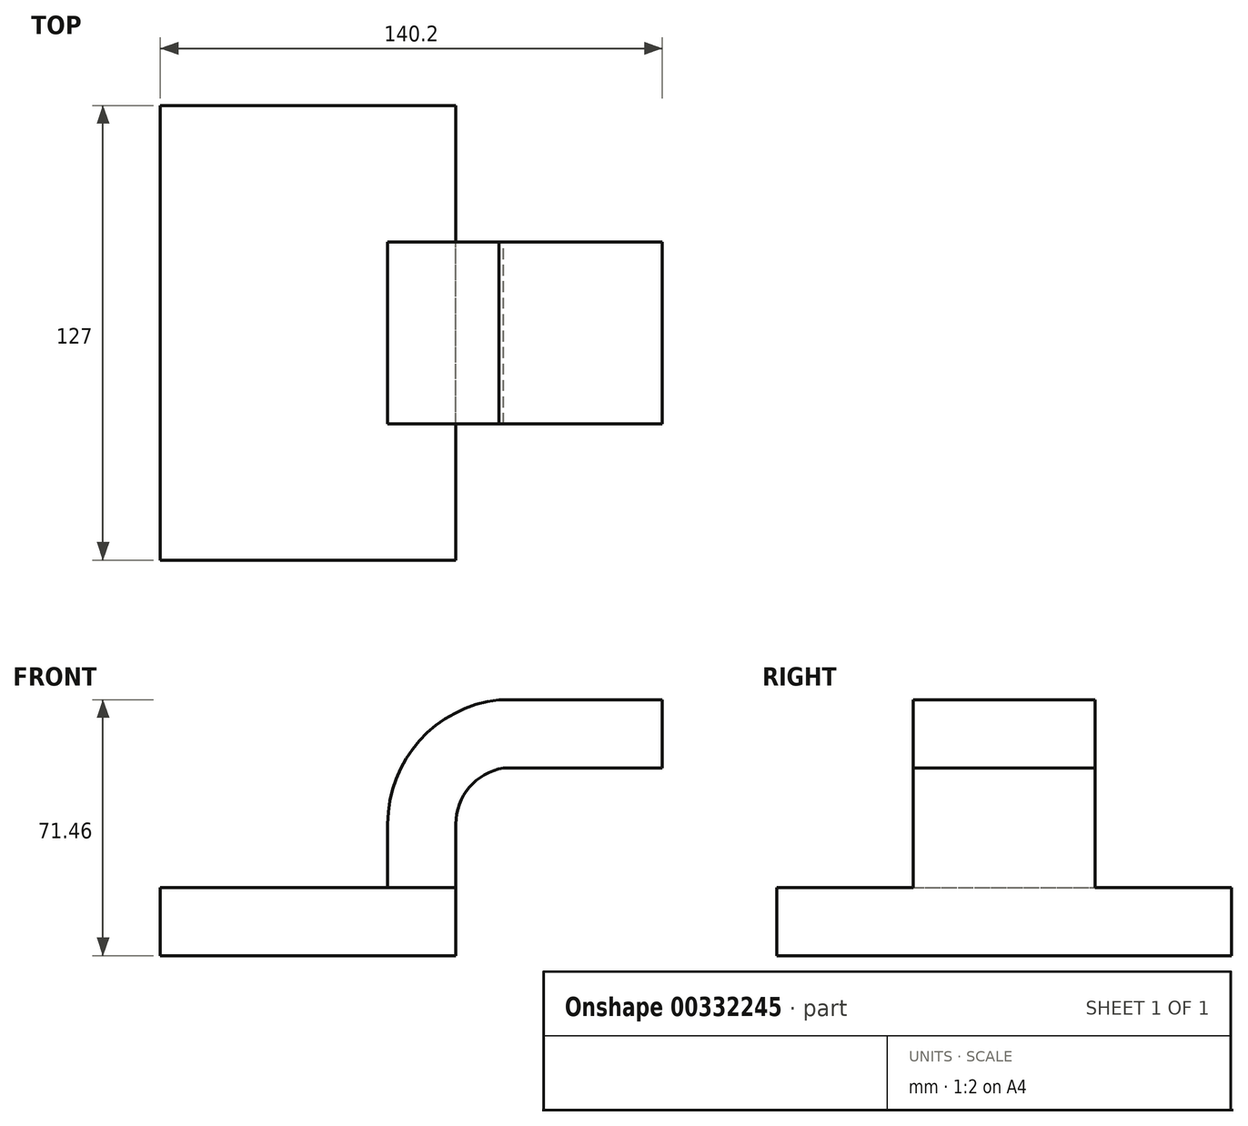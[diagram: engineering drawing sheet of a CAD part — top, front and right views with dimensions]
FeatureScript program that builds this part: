
annotation { "Feature Type Name" : "Feature", "Feature Type Description" : "" }
export const myFeature = defineFeature(function(context is Context, id is Id, definition is map)
    precondition{}
    {
        {
            var Q0;
            Q0=qCreatedBy(makeId("Front.planeOp"),FACE);
            var sketch = newSketch(context, id + "F0", { "sketchPlane" : qUnion([Q0])});
            skLineSegment(sketch, "E0.bottom", {"start": v(-41.28, 9.52) * mm, "end": v(41.27, 9.53) * mm});
            skLineSegment(sketch, "E0.top", {"start": v(-41.28, -9.52) * mm, "end": v(41.28, -9.52) * mm});
            skLineSegment(sketch, "E0.left", {"start": v(-41.28, 9.52) * mm, "end": v(-41.28, -9.53) * mm});
            skLineSegment(sketch, "E0.right", {"start": v(41.27, 9.53) * mm, "end": v(41.28, -9.52) * mm});
            skPoint(sketch, "E0.middle", {"position": v(0, 0) * mm});
            skLineSegment(sketch, "E1", {"start": v(41.27, 9.53) * mm, "end": v(41.27, 27.22) * mm});
            skArc(sketch, "E2", {"start": v(41.27, 27.22) * mm, "mid": v(45.03, 37.47) * mm, "end": v(54.53, 42.88) * mm});
            skLineSegment(sketch, "E3.bottom", {"start": v(111.12, 38.1) * mm, "end": v(60.32, 38.1) * mm});
            skLineSegment(sketch, "E3.top", {"start": v(111.12, 66.68) * mm, "end": v(60.32, 66.68) * mm});
            skLineSegment(sketch, "E3.left", {"start": v(111.12, 38.1) * mm, "end": v(111.12, 66.68) * mm});
            skLineSegment(sketch, "E3.right", {"start": v(60.32, 38.1) * mm, "end": v(60.32, 66.68) * mm});
            skPoint(sketch, "E3.middle", {"position": v(85.72, 52.39) * mm});
            skLineSegment(sketch, "E4", {"start": v(54.53, 42.88) * mm, "end": v(98.92, 42.88) * mm});
            skLineSegment(sketch, "E5.0", {"start": v(53.25, 61.93) * mm, "end": v(98.92, 61.93) * mm});
            skArc(sketch, "E5.1", {"start": v(22.23, 27.22) * mm, "mid": v(31.11, 50.5) * mm, "end": v(53.25, 61.93) * mm});
            skLineSegment(sketch, "E5.2", {"start": v(22.22, 9.53) * mm, "end": v(22.22, 27.22) * mm});
            skLineSegment(sketch, "E6", {"start": v(98.92, 38.1) * mm, "end": v(98.92, 66.68) * mm});
            skFitSpline(sketch, "E7", {"points": [v(-41.28, 9.52) * mm, v(53.25, 61.93) * mm], "startDerivative": vector(47.53, 97.6) * mm, "endDerivative": vector(107.86, 0.75) * mm});
            skSolve(sketch);
        }
        {
            var Q0;
            Q0=makeQuery(id+"F0.imprint","IMPRINT",FACE,{"disambiguationData":[TD([[makeQuery(id+"F0.imprint","IMPRINT",EDGE,{"derivedFrom":sQuery(id+"F0.wireOp",EDGE,"E0.top")}),1.0]])]});
            extrude(context, id + "F1", {"entities" : qUnion([Q0]), "endBound" : BoundingType.SYMMETRIC, "depth" : 127 * mm});
        }
        {
            var Q0;
            {var subQ5=sQuery(id+"F0.wireOp",EDGE,"E1");Q0=makeQuery(id+"F0.imprint","IMPRINT",FACE,{"disambiguationData":[TD([[makeQuery(id+"F0.imprint","IMPRINT",EDGE,{"derivedFrom":subQ5}),1.0]])]});}
            var Q1;
            {var subQ0=sQuery(id+"F0.wireOp",EDGE,"E4");var subQ1=sQuery(id+"F0.wireOp",EDGE,"E3.right");var subQ2=makeQuery(id+"F0.imprint","INTERSECT",VERTEX,{"derivedFrom":[subQ1,subQ0]});Q1=makeQuery(id+"F0.imprint","IMPRINT",FACE,{"disambiguationData":[TD([[makeQuery(id+"F0.imprint","IMPRINT",EDGE,{"disambiguationData":[TD([[subQ2,-1.0]])],"derivedFrom":subQ1}),-1.0]])]});}
            extrude(context, id + "F2", {"entities" : qUnion([Q0, Q1]), "operationType" : NewBodyOperationType.ADD, "endBound" : BoundingType.SYMMETRIC, "depth" : 50.8 * mm});
        }
        {
            var Q0;
            Q0=makeQuery(id+"F0.imprint","IMPRINT",FACE,{"disambiguationData":[TD([[makeQuery(id+"F0.imprint","IMPRINT",EDGE,{"derivedFrom":sQuery(id+"F0.wireOp",EDGE,"E5.1")}),1.0]])]});
            extrude(context, id + "F3", {"entities" : qUnion([Q0]), "operationType" : NewBodyOperationType.ADD, "endBound" : BoundingType.SYMMETRIC, "depth" : 25.4 * mm});
        }
    });
